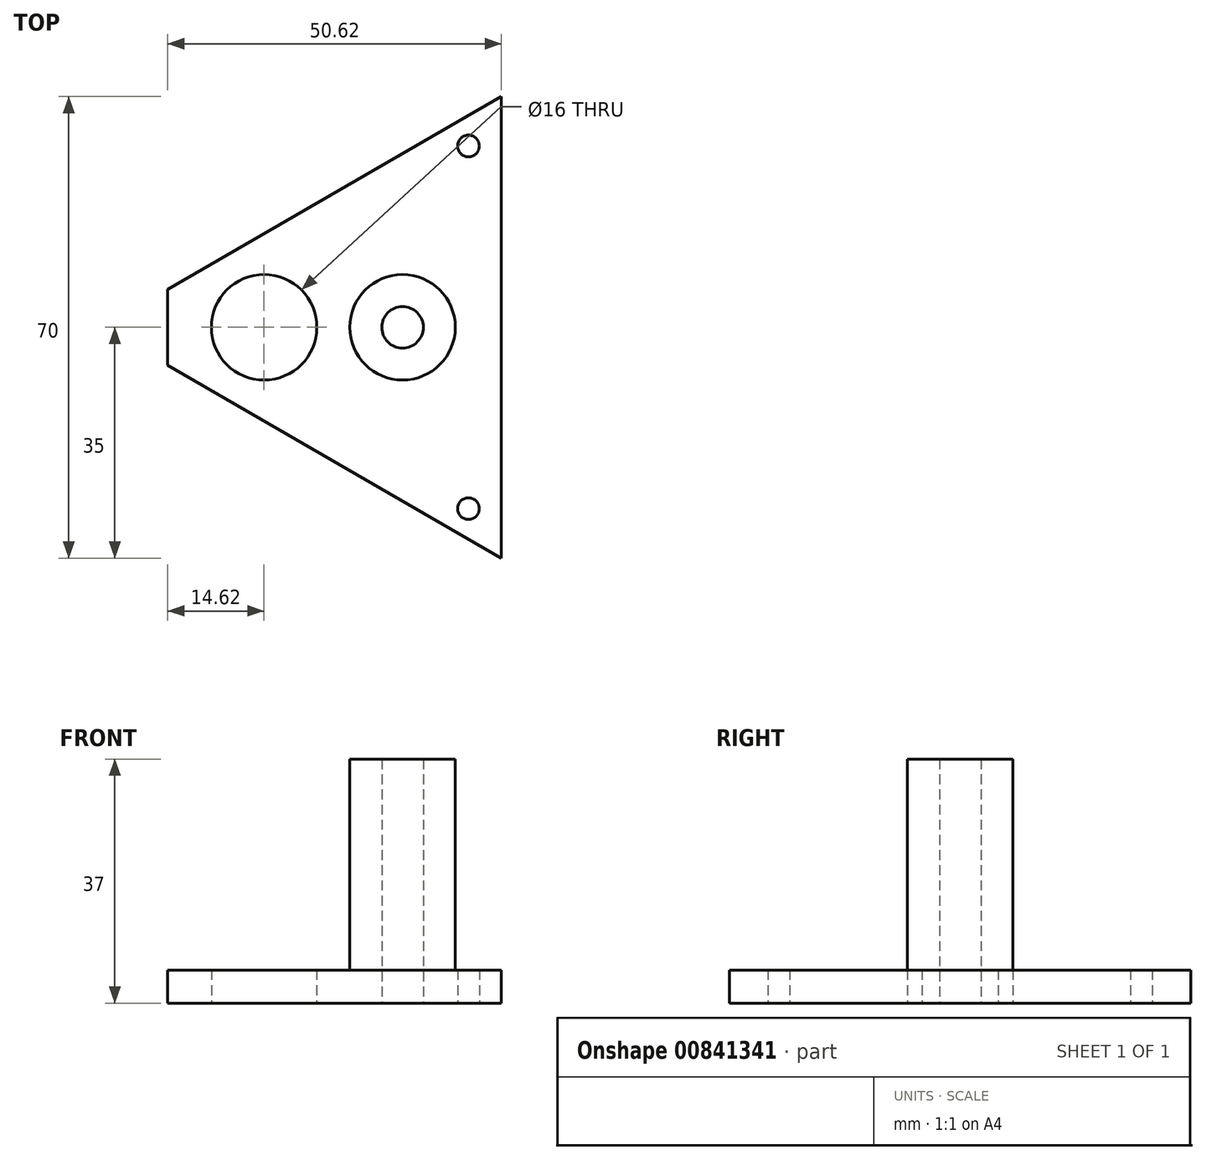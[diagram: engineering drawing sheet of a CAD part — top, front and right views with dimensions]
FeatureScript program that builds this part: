
annotation { "Feature Type Name" : "Feature", "Feature Type Description" : "" }
export const myFeature = defineFeature(function(context is Context, id is Id, definition is map)
    precondition{}
    {
        {
            var Q0;
            Q0=qCreatedBy(makeId("Top.planeOp"),FACE);
            var sketch = newSketch(context, id + "F0", { "sketchPlane" : qUnion([Q0])});
            skLineSegment(sketch, "E0.bottom", {"start": v(0, 0) * mm, "end": v(-60.62, 0) * mm});
            skLineSegment(sketch, "E0.top", {"start": v(0, 70) * mm, "end": v(-60.62, 70) * mm});
            skLineSegment(sketch, "E0.left", {"start": v(0, 0) * mm, "end": v(0, 70) * mm});
            skLineSegment(sketch, "E0.right", {"start": v(-60.62, 0) * mm, "end": v(-60.62, 70) * mm});
            skLineSegment(sketch, "E1", {"start": v(0, 70) * mm, "end": v(-60.62, 35) * mm});
            skLineSegment(sketch, "E2", {"start": v(-60.62, 35) * mm, "end": v(0, 0) * mm});
            skLineSegment(sketch, "E3.bottom", {"start": v(0, 0) * mm, "end": v(-44, 0) * mm});
            skLineSegment(sketch, "E3.top", {"start": v(0, 70) * mm, "end": v(-44, 70) * mm});
            skLineSegment(sketch, "E3.right", {"start": v(-44, 0) * mm, "end": v(-44, 70) * mm});
            skLineSegment(sketch, "E4.top", {"start": v(0, 35) * mm, "end": v(-60.62, 35) * mm});
            skLineSegment(sketch, "E4.left", {"start": v(0, 0) * mm, "end": v(0, 35) * mm});
            skLineSegment(sketch, "E4.right", {"start": v(-60.62, 0) * mm, "end": v(-60.62, 35) * mm});
            skLineSegment(sketch, "E5.bottom", {"start": v(0, 70) * mm, "end": v(-15, 70) * mm});
            skLineSegment(sketch, "E5.top", {"start": v(0, 0) * mm, "end": v(-15, 0) * mm});
            skLineSegment(sketch, "E5.left", {"start": v(0, 70) * mm, "end": v(0, 0) * mm});
            skLineSegment(sketch, "E5.right", {"start": v(-15, 70) * mm, "end": v(-15, 0) * mm});
            skLineSegment(sketch, "E6.bottom", {"start": v(0, 70) * mm, "end": v(-36, 70) * mm});
            skLineSegment(sketch, "E6.top", {"start": v(0, 0) * mm, "end": v(-36, 0) * mm});
            skLineSegment(sketch, "E6.right", {"start": v(-36, 70) * mm, "end": v(-36, 0) * mm});
            skLineSegment(sketch, "E7.bottom", {"start": v(0, 62.5) * mm, "end": v(-5, 62.5) * mm});
            skLineSegment(sketch, "E7.top", {"start": v(0, 7.5) * mm, "end": v(-5, 7.5) * mm});
            skLineSegment(sketch, "E7.left", {"start": v(0, 62.5) * mm, "end": v(0, 7.5) * mm});
            skLineSegment(sketch, "E7.right", {"start": v(-5, 62.5) * mm, "end": v(-5, 7.5) * mm});
            skPoint(sketch, "E7.middle", {"position": v(-2.5, 35) * mm});
            skCircle(sketch, "E8", {"center": v(-15, 35) * mm, "radius": 3.15 * mm});
            skCircle(sketch, "E9", {"center": v(-15, 35) * mm, "radius": 8 * mm});
            skCircle(sketch, "E10", {"center": v(-36, 35) * mm, "radius": 8 * mm});
            skCircle(sketch, "E11", {"center": v(-5, 62.5) * mm, "radius": 1.65 * mm});
            skCircle(sketch, "E12", {"center": v(-5, 7.5) * mm, "radius": 1.65 * mm});
            skLineSegment(sketch, "E13.bottom", {"start": v(0, 0) * mm, "end": v(-50.62, 0) * mm});
            skLineSegment(sketch, "E13.top", {"start": v(0, 70) * mm, "end": v(-50.62, 70) * mm});
            skLineSegment(sketch, "E13.right", {"start": v(-50.62, 0) * mm, "end": v(-50.62, 70) * mm});
            skSolve(sketch);
        }
        {
            var Q0;
            {var subQ0=sQuery(id+"F0.wireOp",EDGE,"E9");var subQ1=sQuery(id+"F0.wireOp",EDGE,"E4.top");var subQ2=makeQuery(id+"F0.imprint","INTERSECT",VERTEX,{"disambiguationData":[OD(0.0)],"derivedFrom":[subQ1,subQ0]});Q0=makeQuery(id+"F0.imprint","IMPRINT",FACE,{"disambiguationData":[TD([[makeQuery(id+"F0.imprint","IMPRINT",EDGE,{"disambiguationData":[TD([[subQ2,1.0]])],"derivedFrom":subQ1}),-1.0]])]});}
            var Q1;
            {var subQ3=sQuery(id+"F0.wireOp",EDGE,"E4.top");var subQ6=sQuery(id+"F0.wireOp",EDGE,"E0.left");var subQ9=makeQuery(id+"F0.imprint","INTERSECT",VERTEX,{"derivedFrom":[subQ6,subQ3]});Q1=makeQuery(id+"F0.imprint","IMPRINT",FACE,{"disambiguationData":[TD([[makeQuery(id+"F0.imprint","IMPRINT",EDGE,{"disambiguationData":[TD([[subQ9,-1.0]])],"derivedFrom":subQ6}),1.0]])]});}
            var Q2;
            {var subQ1=sQuery(id+"F0.wireOp",EDGE,"E0.left");var subQ5=sQuery(id+"F0.wireOp",EDGE,"E4.top");var subQ6=makeQuery(id+"F0.imprint","INTERSECT",VERTEX,{"derivedFrom":[subQ1,subQ5]});Q2=makeQuery(id+"F0.imprint","IMPRINT",FACE,{"disambiguationData":[TD([[makeQuery(id+"F0.imprint","IMPRINT",EDGE,{"disambiguationData":[TD([[subQ6,1.0]])],"derivedFrom":subQ1}),1.0]])]});}
            var Q3;
            {var subQ0=sQuery(id+"F0.wireOp",EDGE,"E9");var subQ5=sQuery(id+"F0.wireOp",EDGE,"E4.top");var subQ6=makeQuery(id+"F0.imprint","INTERSECT",VERTEX,{"disambiguationData":[OD(0.0)],"derivedFrom":[subQ5,subQ0]});Q3=makeQuery(id+"F0.imprint","IMPRINT",FACE,{"disambiguationData":[TD([[makeQuery(id+"F0.imprint","IMPRINT",EDGE,{"disambiguationData":[TD([[subQ6,1.0]])],"derivedFrom":subQ5}),1.0]])]});}
            var Q4;
            {var subQ0=sQuery(id+"F0.wireOp",EDGE,"E6.right");var subQ1=sQuery(id+"F0.wireOp",EDGE,"E2");var subQ2=makeQuery(id+"F0.imprint","INTERSECT",VERTEX,{"derivedFrom":[subQ1,subQ0]});Q4=makeQuery(id+"F0.imprint","IMPRINT",FACE,{"disambiguationData":[TD([[makeQuery(id+"F0.imprint","IMPRINT",EDGE,{"disambiguationData":[TD([[subQ2,-1.0]])],"derivedFrom":subQ1}),1.0]])]});}
            var Q5;
            {var subQ0=sQuery(id+"F0.wireOp",EDGE,"E5.right");var subQ1=sQuery(id+"F0.wireOp",EDGE,"E1");var subQ2=makeQuery(id+"F0.imprint","INTERSECT",VERTEX,{"derivedFrom":[subQ1,subQ0]});Q5=makeQuery(id+"F0.imprint","IMPRINT",FACE,{"disambiguationData":[TD([[makeQuery(id+"F0.imprint","IMPRINT",EDGE,{"disambiguationData":[TD([[subQ2,-1.0]])],"derivedFrom":subQ1}),1.0]])]});}
            var Q6;
            {var subQ0=sQuery(id+"F0.wireOp",EDGE,"E3.right");var subQ1=sQuery(id+"F0.wireOp",EDGE,"E1");var subQ2=makeQuery(id+"F0.imprint","INTERSECT",VERTEX,{"derivedFrom":[subQ1,subQ0]});Q6=makeQuery(id+"F0.imprint","IMPRINT",FACE,{"disambiguationData":[TD([[makeQuery(id+"F0.imprint","IMPRINT",EDGE,{"disambiguationData":[TD([[subQ2,1.0]])],"derivedFrom":subQ1}),1.0]])]});}
            var Q7;
            {var subQ0=sQuery(id+"F0.wireOp",EDGE,"E6.right");var subQ1=sQuery(id+"F0.wireOp",EDGE,"E2");var subQ2=makeQuery(id+"F0.imprint","INTERSECT",VERTEX,{"derivedFrom":[subQ1,subQ0]});Q7=makeQuery(id+"F0.imprint","IMPRINT",FACE,{"disambiguationData":[TD([[makeQuery(id+"F0.imprint","IMPRINT",EDGE,{"disambiguationData":[TD([[subQ2,1.0]])],"derivedFrom":subQ1}),1.0]])]});}
            var Q8;
            {var subQ0=sQuery(id+"F0.wireOp",EDGE,"E3.right");var subQ1=sQuery(id+"F0.wireOp",EDGE,"E2");var subQ2=makeQuery(id+"F0.imprint","INTERSECT",VERTEX,{"derivedFrom":[subQ1,subQ0]});Q8=makeQuery(id+"F0.imprint","IMPRINT",FACE,{"disambiguationData":[TD([[makeQuery(id+"F0.imprint","IMPRINT",EDGE,{"disambiguationData":[TD([[subQ2,1.0]])],"derivedFrom":subQ1}),1.0]])]});}
            var Q9;
            {var subQ0=sQuery(id+"F0.wireOp",EDGE,"E13.right");var subQ1=sQuery(id+"F0.wireOp",EDGE,"E1");var subQ2=makeQuery(id+"F0.imprint","INTERSECT",VERTEX,{"derivedFrom":[subQ1,subQ0]});Q9=makeQuery(id+"F0.imprint","IMPRINT",FACE,{"disambiguationData":[TD([[makeQuery(id+"F0.imprint","IMPRINT",EDGE,{"disambiguationData":[TD([[subQ2,1.0]])],"derivedFrom":subQ1}),1.0]])]});}
            extrude(context, id + "F1", {"entities" : qUnion([Q0, Q1, Q2, Q3, Q4, Q5, Q6, Q7, Q8, Q9]), "depth" : 5 * mm, "offsetDistance" : 25 * mm});
        }
        {
            var Q0;
            {var subQ0=sQuery(id+"F0.wireOp",EDGE,"E9");var subQ1=sQuery(id+"F0.wireOp",EDGE,"E4.top");var subQ2=makeQuery(id+"F0.imprint","INTERSECT",VERTEX,{"disambiguationData":[OD(1.0)],"derivedFrom":[subQ1,subQ0]});Q0=makeQuery(id+"F0.imprint","IMPRINT",FACE,{"disambiguationData":[TD([[makeQuery(id+"F0.imprint","IMPRINT",EDGE,{"disambiguationData":[TD([[subQ2,1.0]])],"derivedFrom":subQ1}),-1.0]])]});}
            var Q1;
            {var subQ0=sQuery(id+"F0.wireOp",EDGE,"E9");var subQ1=sQuery(id+"F0.wireOp",EDGE,"E4.top");var subQ2=makeQuery(id+"F0.imprint","INTERSECT",VERTEX,{"disambiguationData":[OD(0.0)],"derivedFrom":[subQ1,subQ0]});Q1=makeQuery(id+"F0.imprint","IMPRINT",FACE,{"disambiguationData":[TD([[makeQuery(id+"F0.imprint","IMPRINT",EDGE,{"disambiguationData":[TD([[subQ2,-1.0]])],"derivedFrom":subQ1}),-1.0]])]});}
            var Q2;
            {var subQ0=sQuery(id+"F0.wireOp",EDGE,"E9");var subQ1=sQuery(id+"F0.wireOp",EDGE,"E4.top");var subQ2=makeQuery(id+"F0.imprint","INTERSECT",VERTEX,{"disambiguationData":[OD(0.0)],"derivedFrom":[subQ1,subQ0]});Q2=makeQuery(id+"F0.imprint","IMPRINT",FACE,{"disambiguationData":[TD([[makeQuery(id+"F0.imprint","IMPRINT",EDGE,{"disambiguationData":[TD([[subQ2,-1.0]])],"derivedFrom":subQ1}),1.0]])]});}
            var Q3;
            {var subQ0=sQuery(id+"F0.wireOp",EDGE,"E9");var subQ1=sQuery(id+"F0.wireOp",EDGE,"E4.top");var subQ2=makeQuery(id+"F0.imprint","INTERSECT",VERTEX,{"disambiguationData":[OD(1.0)],"derivedFrom":[subQ1,subQ0]});Q3=makeQuery(id+"F0.imprint","IMPRINT",FACE,{"disambiguationData":[TD([[makeQuery(id+"F0.imprint","IMPRINT",EDGE,{"disambiguationData":[TD([[subQ2,1.0]])],"derivedFrom":subQ1}),1.0]])]});}
            extrude(context, id + "F2", {"entities" : qUnion([Q0, Q1, Q2, Q3]), "operationType" : NewBodyOperationType.ADD, "depth" : 37 * mm, "offsetDistance" : 25 * mm});
        }
    });
